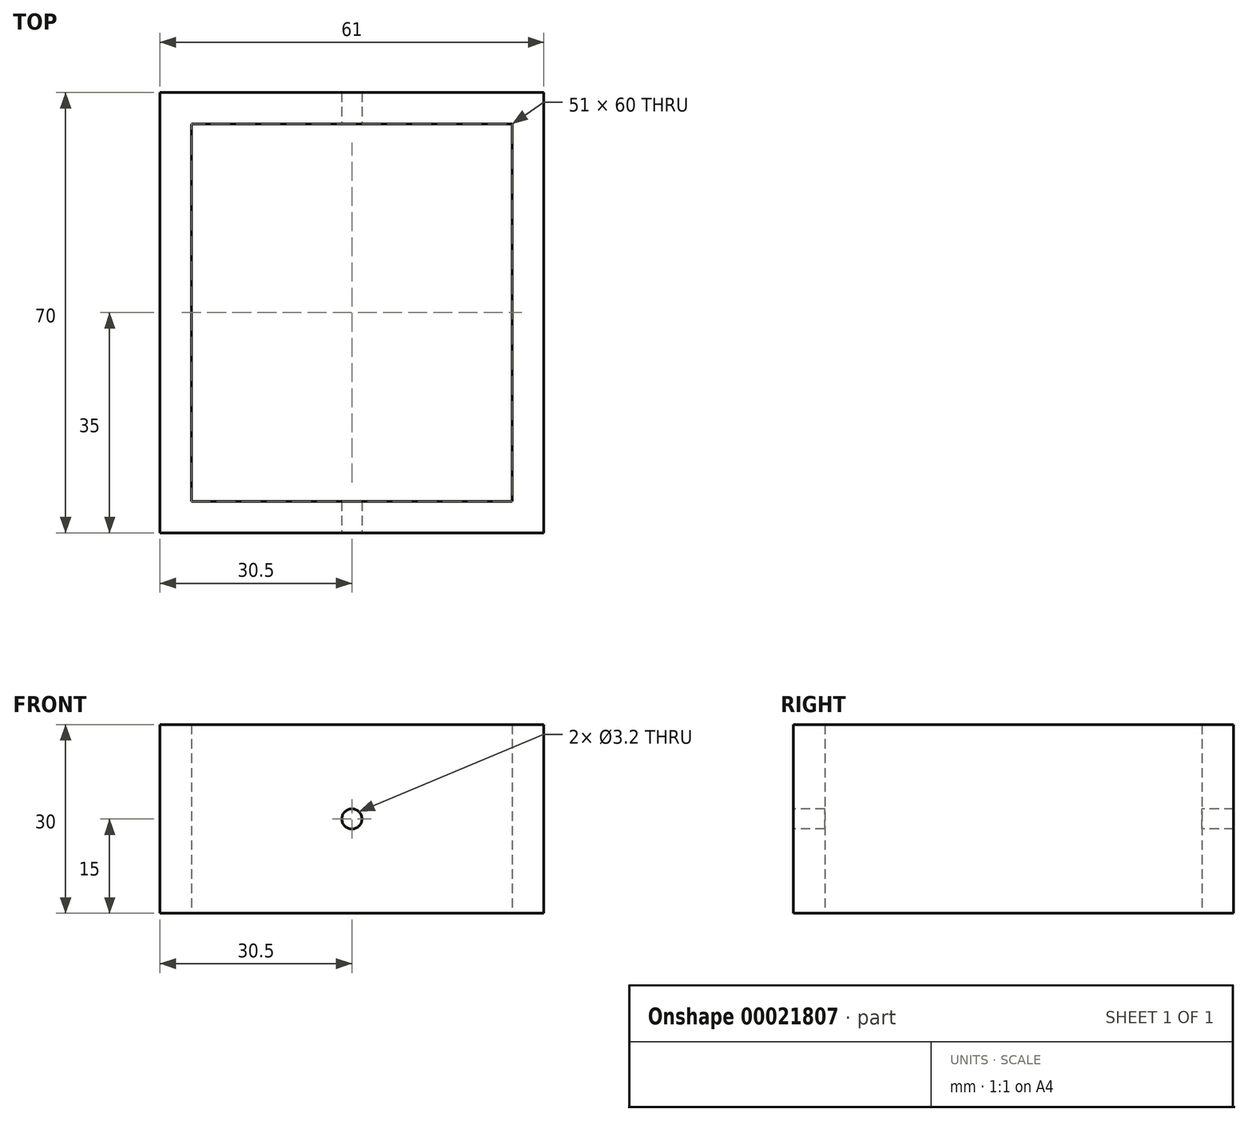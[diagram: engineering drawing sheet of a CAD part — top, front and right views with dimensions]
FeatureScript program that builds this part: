
annotation { "Feature Type Name" : "Feature", "Feature Type Description" : "" }
export const myFeature = defineFeature(function(context is Context, id is Id, definition is map)
    precondition{}
    {
        {
            var Q0;
            Q0=qCreatedBy(makeId("Top.planeOp"),FACE);
            var sketch = newSketch(context, id + "F0", { "sketchPlane" : qUnion([Q0])});
            skLineSegment(sketch, "E0.rect.bottom", {"start": v(25.5, -30) * mm, "end": v(-25.5, -30) * mm});
            skLineSegment(sketch, "E0.rect.top", {"start": v(25.5, 30) * mm, "end": v(-25.5, 30) * mm});
            skLineSegment(sketch, "E0.rect.left", {"start": v(25.5, -30) * mm, "end": v(25.5, 30) * mm});
            skLineSegment(sketch, "E0.rect.right", {"start": v(-25.5, -30) * mm, "end": v(-25.5, 30) * mm});
            skPoint(sketch, "E0.rect.middle", {"position": v(0, 0) * mm});
            skLineSegment(sketch, "E1.rect.bottom", {"start": v(30.5, -35) * mm, "end": v(-30.5, -35) * mm});
            skLineSegment(sketch, "E1.rect.top", {"start": v(30.5, 35) * mm, "end": v(-30.5, 35) * mm});
            skLineSegment(sketch, "E1.rect.left", {"start": v(30.5, -35) * mm, "end": v(30.5, 35) * mm});
            skLineSegment(sketch, "E1.rect.right", {"start": v(-30.5, -35) * mm, "end": v(-30.5, 35) * mm});
            skSolve(sketch);
        }
        {
            var Q0;
            Q0=makeQuery(id+"F0.imprint","IMPRINT",FACE,{"disambiguationData":[TD([[makeQuery(id+"F0.imprint","IMPRINT",EDGE,{"derivedFrom":sQuery(id+"F0.wireOp",EDGE,"E0.rect.bottom")}),1.0]])]});
            extrude(context, id + "F1", {"entities" : qUnion([Q0]), "depth" : 30 * mm});
        }
        {
            var Q0;
            Q0=makeQuery(id+"F1.opExtrude","SWEPT_FACE",FACE,{"disambiguationData":[OSD([sQuery(id+"F0.wireOp",EDGE,"E1.rect.bottom")])]});
            var sketch = newSketch(context, id + "F2", { "sketchPlane" : qUnion([Q0])});
            skCircle(sketch, "E2", {"center": v(0, 15) * mm, "radius": 1.6 * mm});
            skLineSegment(sketch, "E3", {"start": v(-30.5, 15) * mm, "end": v(30.5, 15) * mm, "construction": true});
            skSolve(sketch);
        }
        {
            var Q0;
            Q0 = qSketchRegion(id + "F2", true);
            var Q1;
            Q1=sQuery(id+"F2.wireOp",EDGE,"E2");
            extrude(context, id + "F3", {"entities" : qUnion([Q0]), "operationType" : NewBodyOperationType.REMOVE, "surfaceEntities" : qUnion([Q1]), "oppositeDirection" : true, "depth" : 80 * mm});
        }
    });
